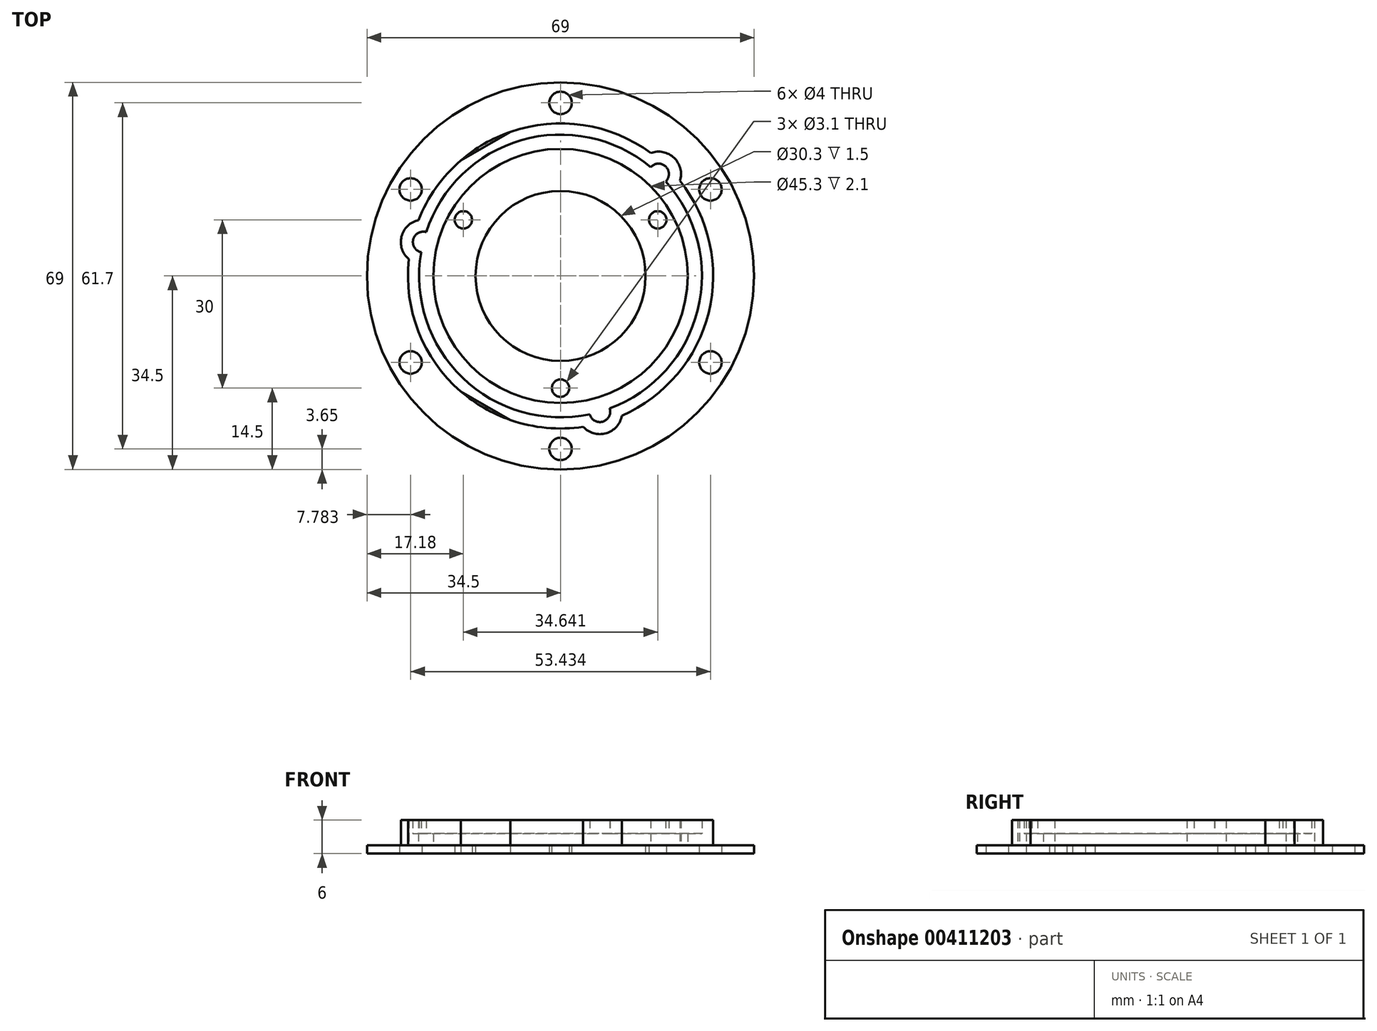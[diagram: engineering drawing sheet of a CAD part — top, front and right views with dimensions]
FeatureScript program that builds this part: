
annotation { "Feature Type Name" : "Feature", "Feature Type Description" : "" }
export const myFeature = defineFeature(function(context is Context, id is Id, definition is map)
    precondition{}
    {
        {
            var Q0;
            Q0=qCreatedBy(makeId("Top.planeOp"),FACE);
            var sketch = newSketch(context, id + "F0", { "sketchPlane" : qUnion([Q0])});
            skCircle(sketch, "E0", {"center": v(0, 0) * mm, "radius": 20 * mm});
            skCircle(sketch, "E1.cCircle", {"center": v(0, 0) * mm, "radius": 20 * mm, "construction": true});
            skCircle(sketch, "E2", {"center": v(0, 0) * mm, "radius": 15.15 * mm});
            skCircle(sketch, "E3", {"center": v(0, 0) * mm, "radius": 0.8 * mm});
            skCircle(sketch, "E4", {"center": v(0, 0) * mm, "radius": 22.65 * mm});
            skCircle(sketch, "E5", {"center": v(0, 0) * mm, "radius": 25.2 * mm});
            skCircle(sketch, "E6", {"center": v(0, 0) * mm, "radius": 27.2 * mm});
            skLineSegment(sketch, "E7.0", {"start": v(0, -20) * mm, "end": v(-17.32, 10) * mm});
            skLineSegment(sketch, "E7.1", {"start": v(-17.32, 10) * mm, "end": v(17.32, 10) * mm});
            skLineSegment(sketch, "E7.2", {"start": v(17.32, 10) * mm, "end": v(0, -20) * mm});
            skCircle(sketch, "E8", {"center": v(-17.32, 10) * mm, "radius": 1.55 * mm});
            skCircle(sketch, "E9", {"center": v(0, -20) * mm, "radius": 1.55 * mm});
            skCircle(sketch, "E10", {"center": v(17.32, 10) * mm, "radius": 1.55 * mm});
            skPoint(sketch, "E11", {"position": v(0, -25.2) * mm});
            skCircle(sketch, "E12.cCircle", {"center": v(0, 0) * mm, "radius": 25.2 * mm, "construction": true});
            skLineSegment(sketch, "E12.0", {"start": v(7, -24.2) * mm, "end": v(-24.46, 6.04) * mm});
            skLineSegment(sketch, "E12.1", {"start": v(-24.46, 6.04) * mm, "end": v(17.46, 18.17) * mm});
            skLineSegment(sketch, "E12.2", {"start": v(17.46, 18.17) * mm, "end": v(7, -24.2) * mm});
            skCircle(sketch, "E13", {"center": v(-24.46, 6.04) * mm, "radius": 1.85 * mm});
            skCircle(sketch, "E14", {"center": v(-24.46, 6.04) * mm, "radius": 4 * mm});
            skCircle(sketch, "E15", {"center": v(17.46, 18.17) * mm, "radius": 1.85 * mm});
            skCircle(sketch, "E16", {"center": v(17.46, 18.17) * mm, "radius": 4 * mm});
            skCircle(sketch, "E17", {"center": v(7, -24.2) * mm, "radius": 1.85 * mm});
            skCircle(sketch, "E18", {"center": v(7, -24.2) * mm, "radius": 4 * mm});
            skCircle(sketch, "E19", {"center": v(0, 0) * mm, "radius": 34.5 * mm});
            skCircle(sketch, "E20", {"center": v(0, 0) * mm, "radius": 30.85 * mm});
            skCircle(sketch, "E21.cCircle", {"center": v(0, 0) * mm, "radius": 30.85 * mm, "construction": true});
            skPoint(sketch, "E21.cCircle.perimeterSnap0", {"position": v(0, 10) * mm});
            skLineSegment(sketch, "E21.0", {"start": v(0, 30.85) * mm, "end": v(26.72, 15.42) * mm});
            skPoint(sketch, "E21.0.startSnap0", {"position": v(0, 10) * mm});
            skLineSegment(sketch, "E21.1", {"start": v(26.72, 15.43) * mm, "end": v(26.72, -15.42) * mm});
            skLineSegment(sketch, "E21.2", {"start": v(26.72, -15.42) * mm, "end": v(0, -30.85) * mm});
            skLineSegment(sketch, "E21.3", {"start": v(0, -30.85) * mm, "end": v(-26.72, -15.43) * mm});
            skLineSegment(sketch, "E21.4", {"start": v(-26.72, -15.43) * mm, "end": v(-26.72, 15.43) * mm});
            skLineSegment(sketch, "E21.5", {"start": v(-26.72, 15.42) * mm, "end": v(0, 30.85) * mm});
            skCircle(sketch, "E22", {"center": v(0, 30.85) * mm, "radius": 2 * mm});
            skCircle(sketch, "E23", {"center": v(26.72, 15.43) * mm, "radius": 2 * mm});
            skCircle(sketch, "E24", {"center": v(26.72, -15.42) * mm, "radius": 2 * mm});
            skCircle(sketch, "E25", {"center": v(0, -30.85) * mm, "radius": 2 * mm});
            skCircle(sketch, "E26", {"center": v(-26.72, -15.43) * mm, "radius": 2 * mm});
            skCircle(sketch, "E27", {"center": v(-26.72, 15.43) * mm, "radius": 2 * mm});
            skSolve(sketch);
        }
        {
            var Q0;
            {var subQ0=sQuery(id+"F0.wireOp",EDGE,"E10");var subQ1=sQuery(id+"F0.wireOp",EDGE,"E0");var subQ3=makeQuery(id+"F0.imprint","INTERSECT",VERTEX,{"disambiguationData":[OD(1.0)],"derivedFrom":[subQ1,subQ0]});Q0=makeQuery(id+"F0.imprint","IMPRINT",FACE,{"disambiguationData":[TD([[makeQuery(id+"F0.imprint","IMPRINT",EDGE,{"disambiguationData":[TD([[subQ3,-1.0]])],"derivedFrom":subQ1}),-1.0]])]});}
            var Q1;
            {var subQ1=sQuery(id+"F0.wireOp",EDGE,"E0");var subQ4=sQuery(id+"F0.wireOp",EDGE,"E12.1");var subQ5=makeQuery(id+"F0.imprint","INTERSECT",VERTEX,{"disambiguationData":[OD(0.0)],"derivedFrom":[subQ1,subQ4]});Q1=makeQuery(id+"F0.imprint","IMPRINT",FACE,{"disambiguationData":[TD([[makeQuery(id+"F0.imprint","IMPRINT",EDGE,{"disambiguationData":[TD([[subQ5,-1.0]])],"derivedFrom":subQ1}),-1.0]])]});}
            var Q2;
            {var subQ1=sQuery(id+"F0.wireOp",EDGE,"E0");var subQ5=sQuery(id+"F0.wireOp",EDGE,"E12.1");var subQ6=makeQuery(id+"F0.imprint","INTERSECT",VERTEX,{"disambiguationData":[OD(0.0)],"derivedFrom":[subQ1,subQ5]});Q2=makeQuery(id+"F0.imprint","IMPRINT",FACE,{"disambiguationData":[TD([[makeQuery(id+"F0.imprint","IMPRINT",EDGE,{"disambiguationData":[TD([[subQ6,-1.0]])],"derivedFrom":subQ1}),1.0]])]});}
            var Q3;
            {var subQ0=sQuery(id+"F0.wireOp",EDGE,"E12.1");var subQ1=sQuery(id+"F0.wireOp",EDGE,"E0");var subQ2=makeQuery(id+"F0.imprint","INTERSECT",VERTEX,{"disambiguationData":[OD(1.0)],"derivedFrom":[subQ1,subQ0]});Q3=makeQuery(id+"F0.imprint","IMPRINT",FACE,{"disambiguationData":[TD([[makeQuery(id+"F0.imprint","IMPRINT",EDGE,{"disambiguationData":[TD([[subQ2,-1.0]])],"derivedFrom":subQ1}),-1.0]])]});}
            var Q4;
            {var subQ6=sQuery(id+"F0.wireOp",EDGE,"E0");var subQ8=sQuery(id+"F0.wireOp",EDGE,"E12.0");var subQ11=makeQuery(id+"F0.imprint","INTERSECT",VERTEX,{"disambiguationData":[OD(0.0)],"derivedFrom":[subQ6,subQ8]});Q4=makeQuery(id+"F0.imprint","IMPRINT",FACE,{"disambiguationData":[TD([[makeQuery(id+"F0.imprint","IMPRINT",EDGE,{"disambiguationData":[TD([[subQ11,-1.0]])],"derivedFrom":subQ6}),-1.0]])]});}
            var Q5;
            {var subQ1=sQuery(id+"F0.wireOp",EDGE,"E0");var subQ5=sQuery(id+"F0.wireOp",EDGE,"E12.0");var subQ9=makeQuery(id+"F0.imprint","INTERSECT",VERTEX,{"disambiguationData":[OD(0.0)],"derivedFrom":[subQ1,subQ5]});Q5=makeQuery(id+"F0.imprint","IMPRINT",FACE,{"disambiguationData":[TD([[makeQuery(id+"F0.imprint","IMPRINT",EDGE,{"disambiguationData":[TD([[subQ9,-1.0]])],"derivedFrom":subQ1}),1.0]])]});}
            var Q6;
            {var subQ0=sQuery(id+"F0.wireOp",EDGE,"E12.1");var subQ1=sQuery(id+"F0.wireOp",EDGE,"E2");var subQ2=makeQuery(id+"F0.imprint","INTERSECT",VERTEX,{"disambiguationData":[OD(1.0)],"derivedFrom":[subQ1,subQ0]});Q6=makeQuery(id+"F0.imprint","IMPRINT",FACE,{"disambiguationData":[TD([[makeQuery(id+"F0.imprint","IMPRINT",EDGE,{"disambiguationData":[TD([[subQ2,-1.0]])],"derivedFrom":subQ1}),-1.0]])]});}
            var Q7;
            {var subQ3=sQuery(id+"F0.wireOp",EDGE,"E7.1");var subQ5=sQuery(id+"F0.wireOp",EDGE,"E2");var subQ6=makeQuery(id+"F0.imprint","INTERSECT",VERTEX,{"disambiguationData":[OD(1.0)],"derivedFrom":[subQ5,subQ3]});Q7=makeQuery(id+"F0.imprint","IMPRINT",FACE,{"disambiguationData":[TD([[makeQuery(id+"F0.imprint","IMPRINT",EDGE,{"disambiguationData":[TD([[subQ6,-1.0]])],"derivedFrom":subQ5}),-1.0]])]});}
            var Q8;
            {var subQ1=sQuery(id+"F0.wireOp",EDGE,"E0");var subQ7=sQuery(id+"F0.wireOp",EDGE,"E12.1");var subQ9=makeQuery(id+"F0.imprint","INTERSECT",VERTEX,{"disambiguationData":[OD(1.0)],"derivedFrom":[subQ1,subQ7]});Q8=makeQuery(id+"F0.imprint","IMPRINT",FACE,{"disambiguationData":[TD([[makeQuery(id+"F0.imprint","IMPRINT",EDGE,{"disambiguationData":[TD([[subQ9,-1.0]])],"derivedFrom":subQ1}),1.0]])]});}
            var Q9;
            {var subQ3=sQuery(id+"F0.wireOp",EDGE,"E12.0");var subQ5=sQuery(id+"F0.wireOp",EDGE,"E0");var subQ6=makeQuery(id+"F0.imprint","INTERSECT",VERTEX,{"disambiguationData":[OD(1.0)],"derivedFrom":[subQ5,subQ3]});Q9=makeQuery(id+"F0.imprint","IMPRINT",FACE,{"disambiguationData":[TD([[makeQuery(id+"F0.imprint","IMPRINT",EDGE,{"disambiguationData":[TD([[subQ6,-1.0]])],"derivedFrom":subQ5}),1.0]])]});}
            var Q10;
            {var subQ0=sQuery(id+"F0.wireOp",EDGE,"E12.0");var subQ1=sQuery(id+"F0.wireOp",EDGE,"E2");var subQ2=makeQuery(id+"F0.imprint","INTERSECT",VERTEX,{"disambiguationData":[OD(1.0)],"derivedFrom":[subQ1,subQ0]});Q10=makeQuery(id+"F0.imprint","IMPRINT",FACE,{"disambiguationData":[TD([[makeQuery(id+"F0.imprint","IMPRINT",EDGE,{"disambiguationData":[TD([[subQ2,-1.0]])],"derivedFrom":subQ1}),-1.0]])]});}
            var Q11;
            {var subQ5=sQuery(id+"F0.wireOp",EDGE,"E7.0");var subQ7=sQuery(id+"F0.wireOp",EDGE,"E2");var subQ8=makeQuery(id+"F0.imprint","INTERSECT",VERTEX,{"disambiguationData":[OD(1.0)],"derivedFrom":[subQ7,subQ5]});Q11=makeQuery(id+"F0.imprint","IMPRINT",FACE,{"disambiguationData":[TD([[makeQuery(id+"F0.imprint","IMPRINT",EDGE,{"disambiguationData":[TD([[subQ8,-1.0]])],"derivedFrom":subQ7}),-1.0]])]});}
            var Q12;
            {var subQ0=sQuery(id+"F0.wireOp",EDGE,"E9");var subQ1=sQuery(id+"F0.wireOp",EDGE,"E0");var subQ2=makeQuery(id+"F0.imprint","INTERSECT",VERTEX,{"disambiguationData":[OD(1.0)],"derivedFrom":[subQ1,subQ0]});Q12=makeQuery(id+"F0.imprint","IMPRINT",FACE,{"disambiguationData":[TD([[makeQuery(id+"F0.imprint","IMPRINT",EDGE,{"disambiguationData":[TD([[subQ2,-1.0]])],"derivedFrom":subQ1}),1.0]])]});}
            var Q13;
            {var subQ1=sQuery(id+"F0.wireOp",EDGE,"E0");var subQ7=sQuery(id+"F0.wireOp",EDGE,"E12.2");var subQ9=makeQuery(id+"F0.imprint","INTERSECT",VERTEX,{"disambiguationData":[OD(0.0)],"derivedFrom":[subQ1,subQ7]});Q13=makeQuery(id+"F0.imprint","IMPRINT",FACE,{"disambiguationData":[TD([[makeQuery(id+"F0.imprint","IMPRINT",EDGE,{"disambiguationData":[TD([[subQ9,-1.0]])],"derivedFrom":subQ1}),1.0]])]});}
            var Q14;
            {var subQ0=sQuery(id+"F0.wireOp",EDGE,"E10");var subQ1=sQuery(id+"F0.wireOp",EDGE,"E0");var subQ2=makeQuery(id+"F0.imprint","INTERSECT",VERTEX,{"disambiguationData":[OD(0.0)],"derivedFrom":[subQ1,subQ0]});Q14=makeQuery(id+"F0.imprint","IMPRINT",FACE,{"disambiguationData":[TD([[makeQuery(id+"F0.imprint","IMPRINT",EDGE,{"disambiguationData":[TD([[subQ2,1.0]])],"derivedFrom":subQ1}),1.0]])]});}
            var Q15;
            {var subQ0=sQuery(id+"F0.wireOp",EDGE,"E12.2");var subQ1=sQuery(id+"F0.wireOp",EDGE,"E2");var subQ2=makeQuery(id+"F0.imprint","INTERSECT",VERTEX,{"disambiguationData":[OD(0.0)],"derivedFrom":[subQ1,subQ0]});Q15=makeQuery(id+"F0.imprint","IMPRINT",FACE,{"disambiguationData":[TD([[makeQuery(id+"F0.imprint","IMPRINT",EDGE,{"disambiguationData":[TD([[subQ2,-1.0]])],"derivedFrom":subQ1}),-1.0]])]});}
            var Q16;
            {var subQ5=sQuery(id+"F0.wireOp",EDGE,"E2");var subQ7=sQuery(id+"F0.wireOp",EDGE,"E12.2");var subQ9=makeQuery(id+"F0.imprint","INTERSECT",VERTEX,{"disambiguationData":[OD(0.0)],"derivedFrom":[subQ5,subQ7]});Q16=makeQuery(id+"F0.imprint","IMPRINT",FACE,{"disambiguationData":[TD([[makeQuery(id+"F0.imprint","IMPRINT",EDGE,{"disambiguationData":[TD([[subQ9,1.0]])],"derivedFrom":subQ5}),-1.0]])]});}
            var Q17;
            {var subQ0=sQuery(id+"F0.wireOp",EDGE,"E10");var subQ1=sQuery(id+"F0.wireOp",EDGE,"E0");var subQ2=makeQuery(id+"F0.imprint","INTERSECT",VERTEX,{"disambiguationData":[OD(1.0)],"derivedFrom":[subQ1,subQ0]});Q17=makeQuery(id+"F0.imprint","IMPRINT",FACE,{"disambiguationData":[TD([[makeQuery(id+"F0.imprint","IMPRINT",EDGE,{"disambiguationData":[TD([[subQ2,-1.0]])],"derivedFrom":subQ1}),1.0]])]});}
            var Q18;
            {var subQ0=sQuery(id+"F0.wireOp",EDGE,"E8");var subQ1=sQuery(id+"F0.wireOp",EDGE,"E0");var subQ2=makeQuery(id+"F0.imprint","INTERSECT",VERTEX,{"disambiguationData":[OD(1.0)],"derivedFrom":[subQ1,subQ0]});Q18=makeQuery(id+"F0.imprint","IMPRINT",FACE,{"disambiguationData":[TD([[makeQuery(id+"F0.imprint","IMPRINT",EDGE,{"disambiguationData":[TD([[subQ2,-1.0]])],"derivedFrom":subQ1}),1.0]])]});}
            var Q19;
            {var subQ0=sQuery(id+"F0.wireOp",EDGE,"E12.0");var subQ1=sQuery(id+"F0.wireOp",EDGE,"E4");var subQ2=makeQuery(id+"F0.imprint","INTERSECT",VERTEX,{"disambiguationData":[OD(0.0)],"derivedFrom":[subQ1,subQ0]});Q19=makeQuery(id+"F0.imprint","IMPRINT",FACE,{"disambiguationData":[TD([[makeQuery(id+"F0.imprint","IMPRINT",EDGE,{"disambiguationData":[TD([[subQ2,-1.0]])],"derivedFrom":subQ1}),1.0]])]});}
            var Q20;
            {var subQ0=sQuery(id+"F0.wireOp",EDGE,"E14");var subQ1=sQuery(id+"F0.wireOp",EDGE,"E4");var subQ2=makeQuery(id+"F0.imprint","INTERSECT",VERTEX,{"disambiguationData":[OD(0.0)],"derivedFrom":[subQ1,subQ0]});Q20=makeQuery(id+"F0.imprint","IMPRINT",FACE,{"disambiguationData":[TD([[makeQuery(id+"F0.imprint","IMPRINT",EDGE,{"disambiguationData":[TD([[subQ2,-1.0]])],"derivedFrom":subQ1}),1.0]])]});}
            var Q21;
            {var subQ0=sQuery(id+"F0.wireOp",EDGE,"E12.1");var subQ1=sQuery(id+"F0.wireOp",EDGE,"E4");var subQ2=makeQuery(id+"F0.imprint","INTERSECT",VERTEX,{"disambiguationData":[OD(1.0)],"derivedFrom":[subQ1,subQ0]});Q21=makeQuery(id+"F0.imprint","IMPRINT",FACE,{"disambiguationData":[TD([[makeQuery(id+"F0.imprint","IMPRINT",EDGE,{"disambiguationData":[TD([[subQ2,-1.0]])],"derivedFrom":subQ1}),1.0]])]});}
            var Q22;
            {var subQ0=sQuery(id+"F0.wireOp",EDGE,"E12.0");var subQ1=sQuery(id+"F0.wireOp",EDGE,"E0");var subQ2=makeQuery(id+"F0.imprint","INTERSECT",VERTEX,{"disambiguationData":[OD(1.0)],"derivedFrom":[subQ1,subQ0]});Q22=makeQuery(id+"F0.imprint","IMPRINT",FACE,{"disambiguationData":[TD([[makeQuery(id+"F0.imprint","IMPRINT",EDGE,{"disambiguationData":[TD([[subQ2,-1.0]])],"derivedFrom":subQ1}),-1.0]])]});}
            var Q23;
            {var subQ0=sQuery(id+"F0.wireOp",EDGE,"E12.0");var subQ1=sQuery(id+"F0.wireOp",EDGE,"E4");var subQ2=makeQuery(id+"F0.imprint","INTERSECT",VERTEX,{"disambiguationData":[OD(1.0)],"derivedFrom":[subQ1,subQ0]});Q23=makeQuery(id+"F0.imprint","IMPRINT",FACE,{"disambiguationData":[TD([[makeQuery(id+"F0.imprint","IMPRINT",EDGE,{"disambiguationData":[TD([[subQ2,-1.0]])],"derivedFrom":subQ1}),1.0]])]});}
            var Q24;
            {var subQ0=sQuery(id+"F0.wireOp",EDGE,"E12.2");var subQ1=sQuery(id+"F0.wireOp",EDGE,"E4");var subQ2=makeQuery(id+"F0.imprint","INTERSECT",VERTEX,{"disambiguationData":[OD(1.0)],"derivedFrom":[subQ1,subQ0]});Q24=makeQuery(id+"F0.imprint","IMPRINT",FACE,{"disambiguationData":[TD([[makeQuery(id+"F0.imprint","IMPRINT",EDGE,{"disambiguationData":[TD([[subQ2,-1.0]])],"derivedFrom":subQ1}),1.0]])]});}
            var Q25;
            {var subQ0=sQuery(id+"F0.wireOp",EDGE,"E18");var subQ1=sQuery(id+"F0.wireOp",EDGE,"E4");var subQ2=makeQuery(id+"F0.imprint","INTERSECT",VERTEX,{"disambiguationData":[OD(0.0)],"derivedFrom":[subQ1,subQ0]});Q25=makeQuery(id+"F0.imprint","IMPRINT",FACE,{"disambiguationData":[TD([[makeQuery(id+"F0.imprint","IMPRINT",EDGE,{"disambiguationData":[TD([[subQ2,-1.0]])],"derivedFrom":subQ1}),1.0]])]});}
            var Q26;
            {var subQ0=sQuery(id+"F0.wireOp",EDGE,"E12.2");var subQ1=sQuery(id+"F0.wireOp",EDGE,"E0");var subQ2=makeQuery(id+"F0.imprint","INTERSECT",VERTEX,{"disambiguationData":[OD(0.0)],"derivedFrom":[subQ1,subQ0]});Q26=makeQuery(id+"F0.imprint","IMPRINT",FACE,{"disambiguationData":[TD([[makeQuery(id+"F0.imprint","IMPRINT",EDGE,{"disambiguationData":[TD([[subQ2,-1.0]])],"derivedFrom":subQ1}),-1.0]])]});}
            var Q27;
            {var subQ0=sQuery(id+"F0.wireOp",EDGE,"E12.2");var subQ1=sQuery(id+"F0.wireOp",EDGE,"E4");var subQ2=makeQuery(id+"F0.imprint","INTERSECT",VERTEX,{"disambiguationData":[OD(0.0)],"derivedFrom":[subQ1,subQ0]});Q27=makeQuery(id+"F0.imprint","IMPRINT",FACE,{"disambiguationData":[TD([[makeQuery(id+"F0.imprint","IMPRINT",EDGE,{"disambiguationData":[TD([[subQ2,-1.0]])],"derivedFrom":subQ1}),1.0]])]});}
            var Q28;
            {var subQ0=sQuery(id+"F0.wireOp",EDGE,"E12.2");var subQ1=sQuery(id+"F0.wireOp",EDGE,"E4");var subQ2=makeQuery(id+"F0.imprint","INTERSECT",VERTEX,{"disambiguationData":[OD(0.0)],"derivedFrom":[subQ1,subQ0]});Q28=makeQuery(id+"F0.imprint","IMPRINT",FACE,{"disambiguationData":[TD([[makeQuery(id+"F0.imprint","IMPRINT",EDGE,{"disambiguationData":[TD([[subQ2,1.0]])],"derivedFrom":subQ1}),1.0]])]});}
            var Q29;
            {var subQ0=sQuery(id+"F0.wireOp",EDGE,"E12.1");var subQ1=sQuery(id+"F0.wireOp",EDGE,"E4");var subQ2=makeQuery(id+"F0.imprint","INTERSECT",VERTEX,{"disambiguationData":[OD(0.0)],"derivedFrom":[subQ1,subQ0]});Q29=makeQuery(id+"F0.imprint","IMPRINT",FACE,{"disambiguationData":[TD([[makeQuery(id+"F0.imprint","IMPRINT",EDGE,{"disambiguationData":[TD([[subQ2,-1.0]])],"derivedFrom":subQ1}),1.0]])]});}
            extrude(context, id + "F1", {"entities" : qUnion([Q0, Q1, Q2, Q3, Q4, Q5, Q6, Q7, Q8, Q9, Q10, Q11, Q12, Q13, Q14, Q15, Q16, Q17, Q18, Q19, Q20, Q21, Q22, Q23, Q24, Q25, Q26, Q27, Q28, Q29]), "depth" : 1.5 * mm});
        }
        {
            var Q0;
            {var subQ0=sQuery(id+"F0.wireOp",EDGE,"E16");var subQ1=sQuery(id+"F0.wireOp",EDGE,"E4");var subQ2=makeQuery(id+"F0.imprint","INTERSECT",VERTEX,{"disambiguationData":[OD(1.0)],"derivedFrom":[subQ1,subQ0]});Q0=makeQuery(id+"F0.imprint","IMPRINT",FACE,{"disambiguationData":[TD([[makeQuery(id+"F0.imprint","IMPRINT",EDGE,{"disambiguationData":[TD([[subQ2,-1.0]])],"derivedFrom":subQ1}),-1.0]])]});}
            var Q1;
            {var subQ0=sQuery(id+"F0.wireOp",EDGE,"E16");var subQ1=sQuery(id+"F0.wireOp",EDGE,"E4");var subQ2=makeQuery(id+"F0.imprint","INTERSECT",VERTEX,{"disambiguationData":[OD(0.0)],"derivedFrom":[subQ1,subQ0]});Q1=makeQuery(id+"F0.imprint","IMPRINT",FACE,{"disambiguationData":[TD([[makeQuery(id+"F0.imprint","IMPRINT",EDGE,{"disambiguationData":[TD([[subQ2,1.0]])],"derivedFrom":subQ1}),-1.0]])]});}
            var Q2;
            {var subQ0=sQuery(id+"F0.wireOp",EDGE,"E14");var subQ1=sQuery(id+"F0.wireOp",EDGE,"E4");var subQ2=makeQuery(id+"F0.imprint","INTERSECT",VERTEX,{"disambiguationData":[OD(1.0)],"derivedFrom":[subQ1,subQ0]});Q2=makeQuery(id+"F0.imprint","IMPRINT",FACE,{"disambiguationData":[TD([[makeQuery(id+"F0.imprint","IMPRINT",EDGE,{"disambiguationData":[TD([[subQ2,-1.0]])],"derivedFrom":subQ1}),-1.0]])]});}
            var Q3;
            {var subQ0=sQuery(id+"F0.wireOp",EDGE,"E12.1");var subQ1=sQuery(id+"F0.wireOp",EDGE,"E4");var subQ2=makeQuery(id+"F0.imprint","INTERSECT",VERTEX,{"disambiguationData":[OD(0.0)],"derivedFrom":[subQ1,subQ0]});Q3=makeQuery(id+"F0.imprint","IMPRINT",FACE,{"disambiguationData":[TD([[makeQuery(id+"F0.imprint","IMPRINT",EDGE,{"disambiguationData":[TD([[subQ2,-1.0]])],"derivedFrom":subQ1}),-1.0]])]});}
            var Q4;
            {var subQ0=sQuery(id+"F0.wireOp",EDGE,"E5");var subQ2=sQuery(id+"F0.wireOp",EDGE,"E15");var subQ3=makeQuery(id+"F0.imprint","INTERSECT",VERTEX,{"disambiguationData":[OD(0.0)],"derivedFrom":[subQ0,subQ2]});Q4=makeQuery(id+"F0.imprint","IMPRINT",FACE,{"disambiguationData":[TD([[makeQuery(id+"F0.imprint","IMPRINT",EDGE,{"disambiguationData":[TD([[subQ3,-1.0]])],"derivedFrom":subQ2}),1.0]])]});}
            var Q5;
            {var subQ3=sQuery(id+"F0.wireOp",EDGE,"E12.2");var subQ5=sQuery(id+"F0.wireOp",EDGE,"E4");var subQ6=makeQuery(id+"F0.imprint","INTERSECT",VERTEX,{"disambiguationData":[OD(0.0)],"derivedFrom":[subQ5,subQ3]});Q5=makeQuery(id+"F0.imprint","IMPRINT",FACE,{"disambiguationData":[TD([[makeQuery(id+"F0.imprint","IMPRINT",EDGE,{"disambiguationData":[TD([[subQ6,1.0]])],"derivedFrom":subQ5}),-1.0]])]});}
            var Q6;
            {var subQ1=sQuery(id+"F0.wireOp",EDGE,"E5");var subQ3=sQuery(id+"F0.wireOp",EDGE,"E15");var subQ4=makeQuery(id+"F0.imprint","INTERSECT",VERTEX,{"disambiguationData":[OD(0.0)],"derivedFrom":[subQ1,subQ3]});Q6=makeQuery(id+"F0.imprint","IMPRINT",FACE,{"disambiguationData":[TD([[makeQuery(id+"F0.imprint","IMPRINT",EDGE,{"disambiguationData":[TD([[subQ4,1.0]])],"derivedFrom":subQ3}),1.0]])]});}
            var Q7;
            {var subQ1=sQuery(id+"F0.wireOp",EDGE,"E12.1");var subQ3=sQuery(id+"F0.wireOp",EDGE,"E15");var subQ4=makeQuery(id+"F0.imprint","INTERSECT",VERTEX,{"derivedFrom":[subQ1,subQ3]});Q7=makeQuery(id+"F0.imprint","IMPRINT",FACE,{"disambiguationData":[TD([[makeQuery(id+"F0.imprint","IMPRINT",EDGE,{"disambiguationData":[TD([[subQ4,-1.0]])],"derivedFrom":subQ3}),1.0]])]});}
            var Q8;
            {var subQ1=sQuery(id+"F0.wireOp",EDGE,"E5");var subQ3=sQuery(id+"F0.wireOp",EDGE,"E15");var subQ4=makeQuery(id+"F0.imprint","INTERSECT",VERTEX,{"disambiguationData":[OD(1.0)],"derivedFrom":[subQ1,subQ3]});Q8=makeQuery(id+"F0.imprint","IMPRINT",FACE,{"disambiguationData":[TD([[makeQuery(id+"F0.imprint","IMPRINT",EDGE,{"disambiguationData":[TD([[subQ4,-1.0]])],"derivedFrom":subQ3}),1.0]])]});}
            var Q9;
            {var subQ0=sQuery(id+"F0.wireOp",EDGE,"E12.2");var subQ1=sQuery(id+"F0.wireOp",EDGE,"E4");var subQ2=makeQuery(id+"F0.imprint","INTERSECT",VERTEX,{"disambiguationData":[OD(0.0)],"derivedFrom":[subQ1,subQ0]});Q9=makeQuery(id+"F0.imprint","IMPRINT",FACE,{"disambiguationData":[TD([[makeQuery(id+"F0.imprint","IMPRINT",EDGE,{"disambiguationData":[TD([[subQ2,-1.0]])],"derivedFrom":subQ1}),-1.0]])]});}
            var Q10;
            {var subQ0=sQuery(id+"F0.wireOp",EDGE,"E5");var subQ2=sQuery(id+"F0.wireOp",EDGE,"E17");var subQ3=makeQuery(id+"F0.imprint","INTERSECT",VERTEX,{"disambiguationData":[OD(0.0)],"derivedFrom":[subQ0,subQ2]});Q10=makeQuery(id+"F0.imprint","IMPRINT",FACE,{"disambiguationData":[TD([[makeQuery(id+"F0.imprint","IMPRINT",EDGE,{"disambiguationData":[TD([[subQ3,-1.0]])],"derivedFrom":subQ2}),1.0]])]});}
            var Q11;
            {var subQ5=sQuery(id+"F0.wireOp",EDGE,"E4");var subQ7=sQuery(id+"F0.wireOp",EDGE,"E18");var subQ9=makeQuery(id+"F0.imprint","INTERSECT",VERTEX,{"disambiguationData":[OD(0.0)],"derivedFrom":[subQ5,subQ7]});Q11=makeQuery(id+"F0.imprint","IMPRINT",FACE,{"disambiguationData":[TD([[makeQuery(id+"F0.imprint","IMPRINT",EDGE,{"disambiguationData":[TD([[subQ9,-1.0]])],"derivedFrom":subQ5}),-1.0]])]});}
            var Q12;
            {var subQ0=sQuery(id+"F0.wireOp",EDGE,"E12.0");var subQ1=sQuery(id+"F0.wireOp",EDGE,"E4");var subQ2=makeQuery(id+"F0.imprint","INTERSECT",VERTEX,{"disambiguationData":[OD(1.0)],"derivedFrom":[subQ1,subQ0]});Q12=makeQuery(id+"F0.imprint","IMPRINT",FACE,{"disambiguationData":[TD([[makeQuery(id+"F0.imprint","IMPRINT",EDGE,{"disambiguationData":[TD([[subQ2,-1.0]])],"derivedFrom":subQ1}),-1.0]])]});}
            var Q13;
            {var subQ1=sQuery(id+"F0.wireOp",EDGE,"E12.0");var subQ3=sQuery(id+"F0.wireOp",EDGE,"E17");var subQ4=makeQuery(id+"F0.imprint","INTERSECT",VERTEX,{"derivedFrom":[subQ1,subQ3]});Q13=makeQuery(id+"F0.imprint","IMPRINT",FACE,{"disambiguationData":[TD([[makeQuery(id+"F0.imprint","IMPRINT",EDGE,{"disambiguationData":[TD([[subQ4,1.0]])],"derivedFrom":subQ3}),1.0]])]});}
            var Q14;
            {var subQ1=sQuery(id+"F0.wireOp",EDGE,"E5");var subQ3=sQuery(id+"F0.wireOp",EDGE,"E17");var subQ4=makeQuery(id+"F0.imprint","INTERSECT",VERTEX,{"disambiguationData":[OD(0.0)],"derivedFrom":[subQ1,subQ3]});Q14=makeQuery(id+"F0.imprint","IMPRINT",FACE,{"disambiguationData":[TD([[makeQuery(id+"F0.imprint","IMPRINT",EDGE,{"disambiguationData":[TD([[subQ4,1.0]])],"derivedFrom":subQ3}),1.0]])]});}
            var Q15;
            {var subQ1=sQuery(id+"F0.wireOp",EDGE,"E5");var subQ3=sQuery(id+"F0.wireOp",EDGE,"E17");var subQ4=makeQuery(id+"F0.imprint","INTERSECT",VERTEX,{"disambiguationData":[OD(1.0)],"derivedFrom":[subQ1,subQ3]});Q15=makeQuery(id+"F0.imprint","IMPRINT",FACE,{"disambiguationData":[TD([[makeQuery(id+"F0.imprint","IMPRINT",EDGE,{"disambiguationData":[TD([[subQ4,-1.0]])],"derivedFrom":subQ3}),1.0]])]});}
            var Q16;
            {var subQ3=sQuery(id+"F0.wireOp",EDGE,"E12.2");var subQ5=sQuery(id+"F0.wireOp",EDGE,"E4");var subQ6=makeQuery(id+"F0.imprint","INTERSECT",VERTEX,{"disambiguationData":[OD(1.0)],"derivedFrom":[subQ5,subQ3]});Q16=makeQuery(id+"F0.imprint","IMPRINT",FACE,{"disambiguationData":[TD([[makeQuery(id+"F0.imprint","IMPRINT",EDGE,{"disambiguationData":[TD([[subQ6,-1.0]])],"derivedFrom":subQ5}),-1.0]])]});}
            var Q17;
            {var subQ0=sQuery(id+"F0.wireOp",EDGE,"E5");var subQ2=sQuery(id+"F0.wireOp",EDGE,"E13");var subQ3=makeQuery(id+"F0.imprint","INTERSECT",VERTEX,{"disambiguationData":[OD(0.0)],"derivedFrom":[subQ0,subQ2]});Q17=makeQuery(id+"F0.imprint","IMPRINT",FACE,{"disambiguationData":[TD([[makeQuery(id+"F0.imprint","IMPRINT",EDGE,{"disambiguationData":[TD([[subQ3,-1.0]])],"derivedFrom":subQ2}),1.0]])]});}
            var Q18;
            {var subQ1=sQuery(id+"F0.wireOp",EDGE,"E5");var subQ3=sQuery(id+"F0.wireOp",EDGE,"E13");var subQ4=makeQuery(id+"F0.imprint","INTERSECT",VERTEX,{"disambiguationData":[OD(0.0)],"derivedFrom":[subQ1,subQ3]});Q18=makeQuery(id+"F0.imprint","IMPRINT",FACE,{"disambiguationData":[TD([[makeQuery(id+"F0.imprint","IMPRINT",EDGE,{"disambiguationData":[TD([[subQ4,1.0]])],"derivedFrom":subQ3}),1.0]])]});}
            var Q19;
            {var subQ1=sQuery(id+"F0.wireOp",EDGE,"E12.0");var subQ3=sQuery(id+"F0.wireOp",EDGE,"E13");var subQ4=makeQuery(id+"F0.imprint","INTERSECT",VERTEX,{"derivedFrom":[subQ1,subQ3]});Q19=makeQuery(id+"F0.imprint","IMPRINT",FACE,{"disambiguationData":[TD([[makeQuery(id+"F0.imprint","IMPRINT",EDGE,{"disambiguationData":[TD([[subQ4,-1.0]])],"derivedFrom":subQ3}),1.0]])]});}
            var Q20;
            {var subQ1=sQuery(id+"F0.wireOp",EDGE,"E5");var subQ3=sQuery(id+"F0.wireOp",EDGE,"E13");var subQ4=makeQuery(id+"F0.imprint","INTERSECT",VERTEX,{"disambiguationData":[OD(1.0)],"derivedFrom":[subQ1,subQ3]});Q20=makeQuery(id+"F0.imprint","IMPRINT",FACE,{"disambiguationData":[TD([[makeQuery(id+"F0.imprint","IMPRINT",EDGE,{"disambiguationData":[TD([[subQ4,-1.0]])],"derivedFrom":subQ3}),1.0]])]});}
            var Q21;
            {var subQ3=sQuery(id+"F0.wireOp",EDGE,"E12.0");var subQ5=sQuery(id+"F0.wireOp",EDGE,"E4");var subQ6=makeQuery(id+"F0.imprint","INTERSECT",VERTEX,{"disambiguationData":[OD(0.0)],"derivedFrom":[subQ5,subQ3]});Q21=makeQuery(id+"F0.imprint","IMPRINT",FACE,{"disambiguationData":[TD([[makeQuery(id+"F0.imprint","IMPRINT",EDGE,{"disambiguationData":[TD([[subQ6,-1.0]])],"derivedFrom":subQ5}),-1.0]])]});}
            var Q22;
            {var subQ0=sQuery(id+"F0.wireOp",EDGE,"E12.1");var subQ1=sQuery(id+"F0.wireOp",EDGE,"E4");var subQ2=makeQuery(id+"F0.imprint","INTERSECT",VERTEX,{"disambiguationData":[OD(1.0)],"derivedFrom":[subQ1,subQ0]});Q22=makeQuery(id+"F0.imprint","IMPRINT",FACE,{"disambiguationData":[TD([[makeQuery(id+"F0.imprint","IMPRINT",EDGE,{"disambiguationData":[TD([[subQ2,-1.0]])],"derivedFrom":subQ1}),-1.0]])]});}
            var Q23;
            {var subQ5=sQuery(id+"F0.wireOp",EDGE,"E14");var subQ7=sQuery(id+"F0.wireOp",EDGE,"E4");var subQ9=makeQuery(id+"F0.imprint","INTERSECT",VERTEX,{"disambiguationData":[OD(0.0)],"derivedFrom":[subQ7,subQ5]});Q23=makeQuery(id+"F0.imprint","IMPRINT",FACE,{"disambiguationData":[TD([[makeQuery(id+"F0.imprint","IMPRINT",EDGE,{"disambiguationData":[TD([[subQ9,-1.0]])],"derivedFrom":subQ7}),-1.0]])]});}
            extrude(context, id + "F2", {"entities" : qUnion([Q0, Q1, Q2, Q3, Q4, Q5, Q6, Q7, Q8, Q9, Q10, Q11, Q12, Q13, Q14, Q15, Q16, Q17, Q18, Q19, Q20, Q21, Q22, Q23]), "operationType" : NewBodyOperationType.ADD, "depth" : 3.6 * mm});
        }
        {
            var Q0;
            {var subQ1=sQuery(id+"F0.wireOp",EDGE,"E5");var subQ4=sQuery(id+"F0.wireOp",EDGE,"E14");var subQ9=makeQuery(id+"F0.imprint","INTERSECT",VERTEX,{"disambiguationData":[OD(0.0)],"derivedFrom":[subQ1,subQ4]});Q0=makeQuery(id+"F0.imprint","IMPRINT",FACE,{"disambiguationData":[TD([[makeQuery(id+"F0.imprint","IMPRINT",EDGE,{"disambiguationData":[TD([[subQ9,-1.0]])],"derivedFrom":subQ1}),-1.0]])]});}
            var Q1;
            {var subQ0=sQuery(id+"F0.wireOp",EDGE,"E14");var subQ1=sQuery(id+"F0.wireOp",EDGE,"E5");var subQ2=makeQuery(id+"F0.imprint","INTERSECT",VERTEX,{"disambiguationData":[OD(1.0)],"derivedFrom":[subQ1,subQ0]});Q1=makeQuery(id+"F0.imprint","IMPRINT",FACE,{"disambiguationData":[TD([[makeQuery(id+"F0.imprint","IMPRINT",EDGE,{"disambiguationData":[TD([[subQ2,-1.0]])],"derivedFrom":subQ1}),-1.0]])]});}
            var Q2;
            {var subQ0=sQuery(id+"F0.wireOp",EDGE,"E18");var subQ5=sQuery(id+"F0.wireOp",EDGE,"E5");var subQ9=makeQuery(id+"F0.imprint","INTERSECT",VERTEX,{"disambiguationData":[OD(0.0)],"derivedFrom":[subQ5,subQ0]});Q2=makeQuery(id+"F0.imprint","IMPRINT",FACE,{"disambiguationData":[TD([[makeQuery(id+"F0.imprint","IMPRINT",EDGE,{"disambiguationData":[TD([[subQ9,-1.0]])],"derivedFrom":subQ5}),-1.0]])]});}
            var Q3;
            {var subQ0=sQuery(id+"F0.wireOp",EDGE,"E16");var subQ1=sQuery(id+"F0.wireOp",EDGE,"E5");var subQ2=makeQuery(id+"F0.imprint","INTERSECT",VERTEX,{"disambiguationData":[OD(0.0)],"derivedFrom":[subQ1,subQ0]});Q3=makeQuery(id+"F0.imprint","IMPRINT",FACE,{"disambiguationData":[TD([[makeQuery(id+"F0.imprint","IMPRINT",EDGE,{"disambiguationData":[TD([[subQ2,1.0]])],"derivedFrom":subQ1}),-1.0]])]});}
            var Q4;
            {var subQ0=sQuery(id+"F0.wireOp",EDGE,"E15");var subQ1=sQuery(id+"F0.wireOp",EDGE,"E5");var subQ2=makeQuery(id+"F0.imprint","INTERSECT",VERTEX,{"disambiguationData":[OD(0.0)],"derivedFrom":[subQ1,subQ0]});Q4=makeQuery(id+"F0.imprint","IMPRINT",FACE,{"disambiguationData":[TD([[makeQuery(id+"F0.imprint","IMPRINT",EDGE,{"disambiguationData":[TD([[subQ2,1.0]])],"derivedFrom":subQ1}),-1.0]])]});}
            var Q5;
            {var subQ0=sQuery(id+"F0.wireOp",EDGE,"E16");var subQ1=sQuery(id+"F0.wireOp",EDGE,"E5");var subQ2=makeQuery(id+"F0.imprint","INTERSECT",VERTEX,{"disambiguationData":[OD(1.0)],"derivedFrom":[subQ1,subQ0]});Q5=makeQuery(id+"F0.imprint","IMPRINT",FACE,{"disambiguationData":[TD([[makeQuery(id+"F0.imprint","IMPRINT",EDGE,{"disambiguationData":[TD([[subQ2,-1.0]])],"derivedFrom":subQ1}),-1.0]])]});}
            var Q6;
            {var subQ0=sQuery(id+"F0.wireOp",EDGE,"E18");var subQ1=sQuery(id+"F0.wireOp",EDGE,"E6");var subQ2=makeQuery(id+"F0.imprint","INTERSECT",VERTEX,{"disambiguationData":[OD(0.0)],"derivedFrom":[subQ1,subQ0]});Q6=makeQuery(id+"F0.imprint","IMPRINT",FACE,{"disambiguationData":[TD([[makeQuery(id+"F0.imprint","IMPRINT",EDGE,{"disambiguationData":[TD([[subQ2,-1.0]])],"derivedFrom":subQ1}),-1.0]])]});}
            var Q7;
            {var subQ0=sQuery(id+"F0.wireOp",EDGE,"E14");var subQ1=sQuery(id+"F0.wireOp",EDGE,"E6");var subQ2=makeQuery(id+"F0.imprint","INTERSECT",VERTEX,{"disambiguationData":[OD(1.0)],"derivedFrom":[subQ1,subQ0]});Q7=makeQuery(id+"F0.imprint","IMPRINT",FACE,{"disambiguationData":[TD([[makeQuery(id+"F0.imprint","IMPRINT",EDGE,{"disambiguationData":[TD([[subQ2,-1.0]])],"derivedFrom":subQ1}),1.0]])]});}
            var Q8;
            {var subQ0=sQuery(id+"F0.wireOp",EDGE,"E21.4");var subQ1=sQuery(id+"F0.wireOp",EDGE,"E6");var subQ2=makeQuery(id+"F0.imprint","INTERSECT",VERTEX,{"disambiguationData":[OD(0.0)],"derivedFrom":[subQ1,subQ0]});Q8=makeQuery(id+"F0.imprint","IMPRINT",FACE,{"disambiguationData":[TD([[makeQuery(id+"F0.imprint","IMPRINT",EDGE,{"disambiguationData":[TD([[subQ2,-1.0]])],"derivedFrom":subQ1}),1.0]])]});}
            var Q9;
            {var subQ0=sQuery(id+"F0.wireOp",EDGE,"E21.4");var subQ1=sQuery(id+"F0.wireOp",EDGE,"E6");var subQ2=makeQuery(id+"F0.imprint","INTERSECT",VERTEX,{"disambiguationData":[OD(0.0)],"derivedFrom":[subQ1,subQ0]});Q9=makeQuery(id+"F0.imprint","IMPRINT",FACE,{"disambiguationData":[TD([[makeQuery(id+"F0.imprint","IMPRINT",EDGE,{"disambiguationData":[TD([[subQ2,-1.0]])],"derivedFrom":subQ1}),-1.0]])]});}
            var Q10;
            {var subQ0=sQuery(id+"F0.wireOp",EDGE,"E14");var subQ1=sQuery(id+"F0.wireOp",EDGE,"E6");var subQ2=makeQuery(id+"F0.imprint","INTERSECT",VERTEX,{"disambiguationData":[OD(0.0)],"derivedFrom":[subQ1,subQ0]});Q10=makeQuery(id+"F0.imprint","IMPRINT",FACE,{"disambiguationData":[TD([[makeQuery(id+"F0.imprint","IMPRINT",EDGE,{"disambiguationData":[TD([[subQ2,-1.0]])],"derivedFrom":subQ1}),-1.0]])]});}
            var Q11;
            {var subQ0=sQuery(id+"F0.wireOp",EDGE,"E21.2");var subQ1=sQuery(id+"F0.wireOp",EDGE,"E6");var subQ2=makeQuery(id+"F0.imprint","INTERSECT",VERTEX,{"disambiguationData":[OD(0.0)],"derivedFrom":[subQ1,subQ0]});Q11=makeQuery(id+"F0.imprint","IMPRINT",FACE,{"disambiguationData":[TD([[makeQuery(id+"F0.imprint","IMPRINT",EDGE,{"disambiguationData":[TD([[subQ2,-1.0]])],"derivedFrom":subQ1}),-1.0]])]});}
            var Q12;
            {var subQ0=sQuery(id+"F0.wireOp",EDGE,"E21.2");var subQ1=sQuery(id+"F0.wireOp",EDGE,"E6");var subQ2=makeQuery(id+"F0.imprint","INTERSECT",VERTEX,{"disambiguationData":[OD(0.0)],"derivedFrom":[subQ1,subQ0]});Q12=makeQuery(id+"F0.imprint","IMPRINT",FACE,{"disambiguationData":[TD([[makeQuery(id+"F0.imprint","IMPRINT",EDGE,{"disambiguationData":[TD([[subQ2,-1.0]])],"derivedFrom":subQ1}),1.0]])]});}
            var Q13;
            {var subQ0=sQuery(id+"F0.wireOp",EDGE,"E21.0");var subQ1=sQuery(id+"F0.wireOp",EDGE,"E6");var subQ2=makeQuery(id+"F0.imprint","INTERSECT",VERTEX,{"disambiguationData":[OD(0.0)],"derivedFrom":[subQ1,subQ0]});Q13=makeQuery(id+"F0.imprint","IMPRINT",FACE,{"disambiguationData":[TD([[makeQuery(id+"F0.imprint","IMPRINT",EDGE,{"disambiguationData":[TD([[subQ2,-1.0]])],"derivedFrom":subQ1}),1.0]])]});}
            var Q14;
            {var subQ0=sQuery(id+"F0.wireOp",EDGE,"E21.0");var subQ1=sQuery(id+"F0.wireOp",EDGE,"E6");var subQ2=makeQuery(id+"F0.imprint","INTERSECT",VERTEX,{"disambiguationData":[OD(0.0)],"derivedFrom":[subQ1,subQ0]});Q14=makeQuery(id+"F0.imprint","IMPRINT",FACE,{"disambiguationData":[TD([[makeQuery(id+"F0.imprint","IMPRINT",EDGE,{"disambiguationData":[TD([[subQ2,-1.0]])],"derivedFrom":subQ1}),-1.0]])]});}
            var Q15;
            {var subQ0=sQuery(id+"F0.wireOp",EDGE,"E16");var subQ1=sQuery(id+"F0.wireOp",EDGE,"E6");var subQ2=makeQuery(id+"F0.imprint","INTERSECT",VERTEX,{"disambiguationData":[OD(0.0)],"derivedFrom":[subQ1,subQ0]});Q15=makeQuery(id+"F0.imprint","IMPRINT",FACE,{"disambiguationData":[TD([[makeQuery(id+"F0.imprint","IMPRINT",EDGE,{"disambiguationData":[TD([[subQ2,-1.0]])],"derivedFrom":subQ1}),-1.0]])]});}
            var Q16;
            {var subQ0=sQuery(id+"F0.wireOp",EDGE,"E21.1");var subQ1=sQuery(id+"F0.wireOp",EDGE,"E6");var subQ2=makeQuery(id+"F0.imprint","INTERSECT",VERTEX,{"disambiguationData":[OD(0.0)],"derivedFrom":[subQ1,subQ0]});Q16=makeQuery(id+"F0.imprint","IMPRINT",FACE,{"disambiguationData":[TD([[makeQuery(id+"F0.imprint","IMPRINT",EDGE,{"disambiguationData":[TD([[subQ2,1.0]])],"derivedFrom":subQ1}),1.0]])]});}
            var Q17;
            {var subQ0=sQuery(id+"F0.wireOp",EDGE,"E21.3");var subQ1=sQuery(id+"F0.wireOp",EDGE,"E6");var subQ2=makeQuery(id+"F0.imprint","INTERSECT",VERTEX,{"disambiguationData":[OD(0.0)],"derivedFrom":[subQ1,subQ0]});Q17=makeQuery(id+"F0.imprint","IMPRINT",FACE,{"disambiguationData":[TD([[makeQuery(id+"F0.imprint","IMPRINT",EDGE,{"disambiguationData":[TD([[subQ2,-1.0]])],"derivedFrom":subQ1}),1.0]])]});}
            var Q18;
            {var subQ0=sQuery(id+"F0.wireOp",EDGE,"E18");var subQ1=sQuery(id+"F0.wireOp",EDGE,"E6");var subQ2=makeQuery(id+"F0.imprint","INTERSECT",VERTEX,{"disambiguationData":[OD(1.0)],"derivedFrom":[subQ1,subQ0]});Q18=makeQuery(id+"F0.imprint","IMPRINT",FACE,{"disambiguationData":[TD([[makeQuery(id+"F0.imprint","IMPRINT",EDGE,{"disambiguationData":[TD([[subQ2,-1.0]])],"derivedFrom":subQ1}),1.0]])]});}
            var Q19;
            {var subQ0=sQuery(id+"F0.wireOp",EDGE,"E21.5");var subQ1=sQuery(id+"F0.wireOp",EDGE,"E6");var subQ2=makeQuery(id+"F0.imprint","INTERSECT",VERTEX,{"disambiguationData":[OD(0.0)],"derivedFrom":[subQ1,subQ0]});Q19=makeQuery(id+"F0.imprint","IMPRINT",FACE,{"disambiguationData":[TD([[makeQuery(id+"F0.imprint","IMPRINT",EDGE,{"disambiguationData":[TD([[subQ2,-1.0]])],"derivedFrom":subQ1}),1.0]])]});}
            var Q20;
            {var subQ0=sQuery(id+"F0.wireOp",EDGE,"E16");var subQ1=sQuery(id+"F0.wireOp",EDGE,"E6");var subQ2=makeQuery(id+"F0.imprint","INTERSECT",VERTEX,{"disambiguationData":[OD(1.0)],"derivedFrom":[subQ1,subQ0]});Q20=makeQuery(id+"F0.imprint","IMPRINT",FACE,{"disambiguationData":[TD([[makeQuery(id+"F0.imprint","IMPRINT",EDGE,{"disambiguationData":[TD([[subQ2,-1.0]])],"derivedFrom":subQ1}),1.0]])]});}
            extrude(context, id + "F3", {"entities" : qUnion([Q0, Q1, Q2, Q3, Q4, Q5, Q6, Q7, Q8, Q9, Q10, Q11, Q12, Q13, Q14, Q15, Q16, Q17, Q18, Q19, Q20]), "operationType" : NewBodyOperationType.ADD, "depth" : 6 * mm});
        }
        {
            var Q0;
            Q0=makeQuery(id+"F0.imprint","IMPRINT",FACE,{"disambiguationData":[TD([[makeQuery(id+"F0.imprint","IMPRINT",EDGE,{"derivedFrom":sQuery(id+"F0.wireOp",EDGE,"E19")}),1.0]])]});
            var Q1;
            {var subQ0=sQuery(id+"F0.wireOp",EDGE,"E21.5");var subQ1=sQuery(id+"F0.wireOp",EDGE,"E6");var subQ9=makeQuery(id+"F0.imprint","INTERSECT",VERTEX,{"disambiguationData":[OD(0.0)],"derivedFrom":[subQ1,subQ0]});Q1=makeQuery(id+"F0.imprint","IMPRINT",FACE,{"disambiguationData":[TD([[makeQuery(id+"F0.imprint","IMPRINT",EDGE,{"disambiguationData":[TD([[subQ9,-1.0]])],"derivedFrom":subQ1}),-1.0]])]});}
            var Q2;
            {var subQ0=sQuery(id+"F0.wireOp",EDGE,"E21.0");var subQ1=sQuery(id+"F0.wireOp",EDGE,"E6");var subQ2=makeQuery(id+"F0.imprint","INTERSECT",VERTEX,{"disambiguationData":[OD(1.0)],"derivedFrom":[subQ1,subQ0]});Q2=makeQuery(id+"F0.imprint","IMPRINT",FACE,{"disambiguationData":[TD([[makeQuery(id+"F0.imprint","IMPRINT",EDGE,{"disambiguationData":[TD([[subQ2,-1.0]])],"derivedFrom":subQ1}),-1.0]])]});}
            var Q3;
            {var subQ1=sQuery(id+"F0.wireOp",EDGE,"E6");var subQ5=sQuery(id+"F0.wireOp",EDGE,"E16");var subQ6=makeQuery(id+"F0.imprint","INTERSECT",VERTEX,{"disambiguationData":[OD(1.0)],"derivedFrom":[subQ1,subQ5]});Q3=makeQuery(id+"F0.imprint","IMPRINT",FACE,{"disambiguationData":[TD([[makeQuery(id+"F0.imprint","IMPRINT",EDGE,{"disambiguationData":[TD([[subQ6,-1.0]])],"derivedFrom":subQ1}),-1.0]])]});}
            var Q4;
            {var subQ1=sQuery(id+"F0.wireOp",EDGE,"E6");var subQ7=sQuery(id+"F0.wireOp",EDGE,"E16");var subQ9=makeQuery(id+"F0.imprint","INTERSECT",VERTEX,{"disambiguationData":[OD(0.0)],"derivedFrom":[subQ1,subQ7]});Q4=makeQuery(id+"F0.imprint","IMPRINT",FACE,{"disambiguationData":[TD([[makeQuery(id+"F0.imprint","IMPRINT",EDGE,{"disambiguationData":[TD([[subQ9,1.0]])],"derivedFrom":subQ1}),-1.0]])]});}
            var Q5;
            {var subQ0=sQuery(id+"F0.wireOp",EDGE,"E21.1");var subQ1=sQuery(id+"F0.wireOp",EDGE,"E6");var subQ9=makeQuery(id+"F0.imprint","INTERSECT",VERTEX,{"disambiguationData":[OD(0.0)],"derivedFrom":[subQ1,subQ0]});Q5=makeQuery(id+"F0.imprint","IMPRINT",FACE,{"disambiguationData":[TD([[makeQuery(id+"F0.imprint","IMPRINT",EDGE,{"disambiguationData":[TD([[subQ9,1.0]])],"derivedFrom":subQ1}),-1.0]])]});}
            var Q6;
            {var subQ0=sQuery(id+"F0.wireOp",EDGE,"E21.2");var subQ1=sQuery(id+"F0.wireOp",EDGE,"E6");var subQ2=makeQuery(id+"F0.imprint","INTERSECT",VERTEX,{"disambiguationData":[OD(1.0)],"derivedFrom":[subQ1,subQ0]});Q6=makeQuery(id+"F0.imprint","IMPRINT",FACE,{"disambiguationData":[TD([[makeQuery(id+"F0.imprint","IMPRINT",EDGE,{"disambiguationData":[TD([[subQ2,-1.0]])],"derivedFrom":subQ1}),-1.0]])]});}
            var Q7;
            {var subQ5=sQuery(id+"F0.wireOp",EDGE,"E18");var subQ6=sQuery(id+"F0.wireOp",EDGE,"E6");var subQ7=makeQuery(id+"F0.imprint","INTERSECT",VERTEX,{"disambiguationData":[OD(1.0)],"derivedFrom":[subQ6,subQ5]});Q7=makeQuery(id+"F0.imprint","IMPRINT",FACE,{"disambiguationData":[TD([[makeQuery(id+"F0.imprint","IMPRINT",EDGE,{"disambiguationData":[TD([[subQ7,-1.0]])],"derivedFrom":subQ6}),-1.0]])]});}
            var Q8;
            {var subQ0=sQuery(id+"F0.wireOp",EDGE,"E21.3");var subQ1=sQuery(id+"F0.wireOp",EDGE,"E6");var subQ2=makeQuery(id+"F0.imprint","INTERSECT",VERTEX,{"disambiguationData":[OD(0.0)],"derivedFrom":[subQ1,subQ0]});Q8=makeQuery(id+"F0.imprint","IMPRINT",FACE,{"disambiguationData":[TD([[makeQuery(id+"F0.imprint","IMPRINT",EDGE,{"disambiguationData":[TD([[subQ2,-1.0]])],"derivedFrom":subQ1}),-1.0]])]});}
            var Q9;
            {var subQ0=sQuery(id+"F0.wireOp",EDGE,"E21.3");var subQ1=sQuery(id+"F0.wireOp",EDGE,"E6");var subQ2=makeQuery(id+"F0.imprint","INTERSECT",VERTEX,{"disambiguationData":[OD(1.0)],"derivedFrom":[subQ1,subQ0]});Q9=makeQuery(id+"F0.imprint","IMPRINT",FACE,{"disambiguationData":[TD([[makeQuery(id+"F0.imprint","IMPRINT",EDGE,{"disambiguationData":[TD([[subQ2,-1.0]])],"derivedFrom":subQ1}),-1.0]])]});}
            var Q10;
            {var subQ0=sQuery(id+"F0.wireOp",EDGE,"E21.4");var subQ1=sQuery(id+"F0.wireOp",EDGE,"E6");var subQ2=makeQuery(id+"F0.imprint","INTERSECT",VERTEX,{"disambiguationData":[OD(1.0)],"derivedFrom":[subQ1,subQ0]});Q10=makeQuery(id+"F0.imprint","IMPRINT",FACE,{"disambiguationData":[TD([[makeQuery(id+"F0.imprint","IMPRINT",EDGE,{"disambiguationData":[TD([[subQ2,-1.0]])],"derivedFrom":subQ1}),-1.0]])]});}
            var Q11;
            {var subQ1=sQuery(id+"F0.wireOp",EDGE,"E6");var subQ10=sQuery(id+"F0.wireOp",EDGE,"E14");var subQ11=makeQuery(id+"F0.imprint","INTERSECT",VERTEX,{"disambiguationData":[OD(1.0)],"derivedFrom":[subQ1,subQ10]});Q11=makeQuery(id+"F0.imprint","IMPRINT",FACE,{"disambiguationData":[TD([[makeQuery(id+"F0.imprint","IMPRINT",EDGE,{"disambiguationData":[TD([[subQ11,-1.0]])],"derivedFrom":subQ1}),-1.0]])]});}
            var Q12;
            {var subQ0=sQuery(id+"F0.wireOp",EDGE,"E21.5");var subQ1=sQuery(id+"F0.wireOp",EDGE,"E6");var subQ2=makeQuery(id+"F0.imprint","INTERSECT",VERTEX,{"disambiguationData":[OD(1.0)],"derivedFrom":[subQ1,subQ0]});Q12=makeQuery(id+"F0.imprint","IMPRINT",FACE,{"disambiguationData":[TD([[makeQuery(id+"F0.imprint","IMPRINT",EDGE,{"disambiguationData":[TD([[subQ2,-1.0]])],"derivedFrom":subQ1}),-1.0]])]});}
            extrude(context, id + "F4", {"entities" : qUnion([Q0, Q1, Q2, Q3, Q4, Q5, Q6, Q7, Q8, Q9, Q10, Q11, Q12]), "operationType" : NewBodyOperationType.ADD, "depth" : 1.5 * mm});
        }
    });
